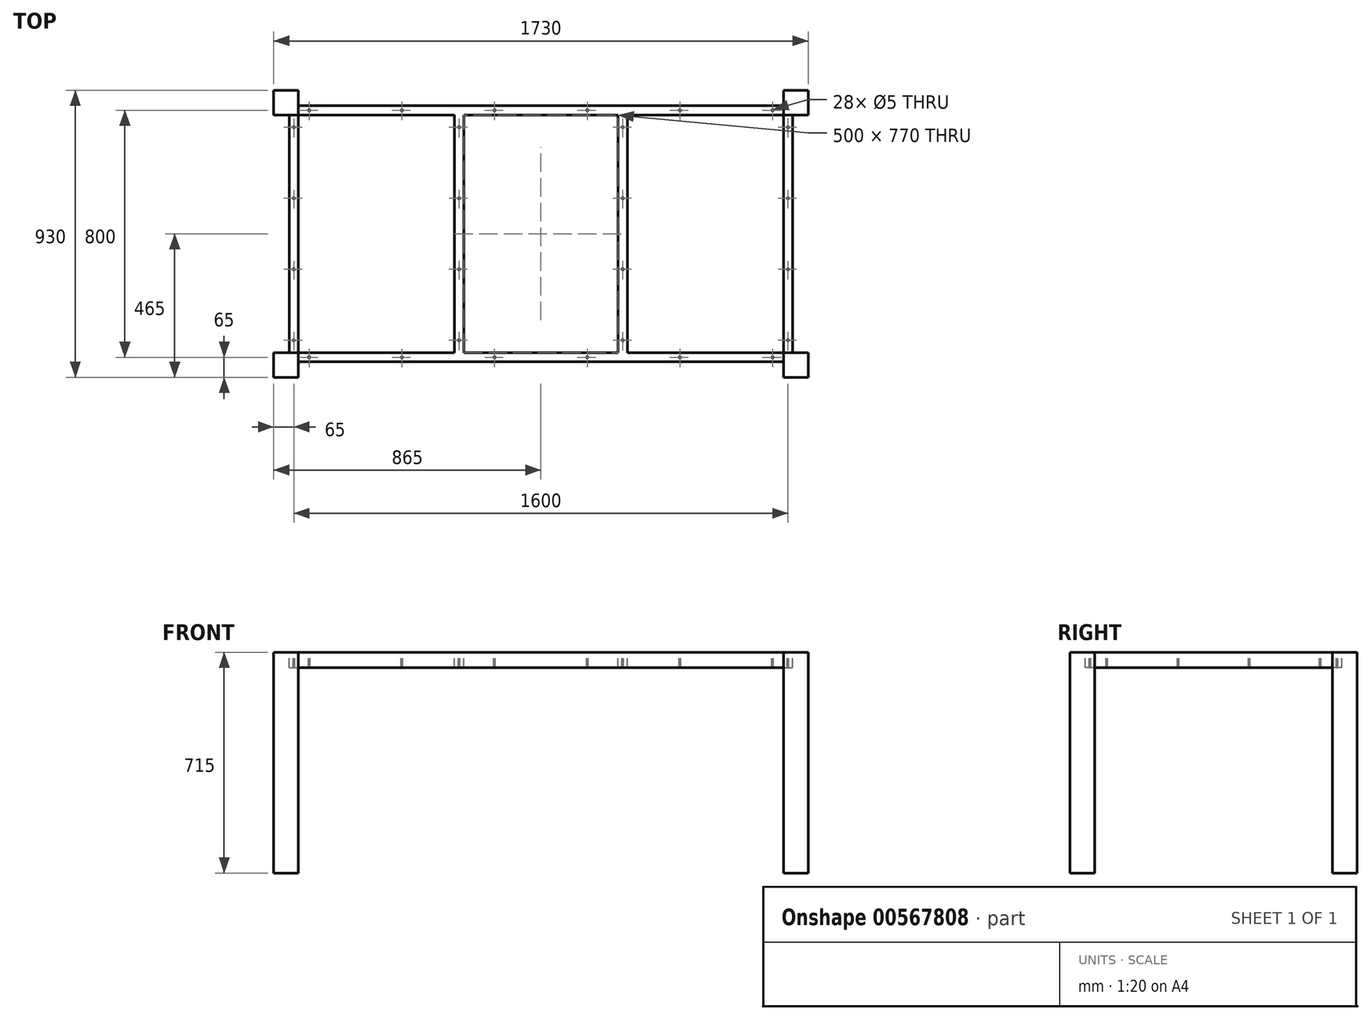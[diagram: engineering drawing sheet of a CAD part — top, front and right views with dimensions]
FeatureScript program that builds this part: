
annotation { "Feature Type Name" : "Feature", "Feature Type Description" : "" }
export const myFeature = defineFeature(function(context is Context, id is Id, definition is map)
    precondition{}
    {
        {
            var Q0;
            Q0=qCreatedBy(makeId("Top.planeOp"),FACE);
            var sketch = newSketch(context, id + "F0", { "sketchPlane" : qUnion([Q0])});
            skLineSegment(sketch, "E0.bottom", {"start": v(-815, 415) * mm, "end": v(815, 415) * mm});
            skLineSegment(sketch, "E0.top", {"start": v(-815, -415) * mm, "end": v(815, -415) * mm});
            skLineSegment(sketch, "E0.left", {"start": v(-815, 415) * mm, "end": v(-815, -415) * mm});
            skLineSegment(sketch, "E0.right", {"start": v(815, 415) * mm, "end": v(815, -415) * mm});
            skPoint(sketch, "E0.middle", {"position": v(0, 0) * mm});
            skLineSegment(sketch, "E1.bottom", {"start": v(-800, 400) * mm, "end": v(800, 400) * mm, "construction": true});
            skLineSegment(sketch, "E1.top", {"start": v(-800, -400) * mm, "end": v(800, -400) * mm, "construction": true});
            skLineSegment(sketch, "E1.left", {"start": v(-800, 400) * mm, "end": v(-800, -400) * mm, "construction": true});
            skLineSegment(sketch, "E1.right", {"start": v(800, 400) * mm, "end": v(800, -400) * mm, "construction": true});
            skLineSegment(sketch, "E2.bottom", {"start": v(-785, 385) * mm, "end": v(785, 385) * mm});
            skLineSegment(sketch, "E2.top", {"start": v(-785, -385) * mm, "end": v(785, -385) * mm});
            skLineSegment(sketch, "E2.left", {"start": v(-785, 385) * mm, "end": v(-785, -385) * mm});
            skLineSegment(sketch, "E2.right", {"start": v(785, 385) * mm, "end": v(785, -385) * mm});
            skLineSegment(sketch, "E3.bottom", {"start": v(785, -385) * mm, "end": v(865, -385) * mm});
            skLineSegment(sketch, "E3.top", {"start": v(785, -465) * mm, "end": v(865, -465) * mm});
            skLineSegment(sketch, "E3.left", {"start": v(785, -385) * mm, "end": v(785, -465) * mm});
            skLineSegment(sketch, "E3.right", {"start": v(865, -385) * mm, "end": v(865, -465) * mm});
            skLineSegment(sketch, "E4.bottom", {"start": v(-865, 465) * mm, "end": v(-785, 465) * mm});
            skLineSegment(sketch, "E4.top", {"start": v(-865, 385) * mm, "end": v(-785, 385) * mm});
            skLineSegment(sketch, "E4.left", {"start": v(-865, 465) * mm, "end": v(-865, 385) * mm});
            skLineSegment(sketch, "E4.right", {"start": v(-785, 465) * mm, "end": v(-785, 385) * mm});
            skLineSegment(sketch, "E5.bottom", {"start": v(785, 465) * mm, "end": v(865, 465) * mm});
            skLineSegment(sketch, "E5.top", {"start": v(785, 385) * mm, "end": v(865, 385) * mm});
            skLineSegment(sketch, "E5.left", {"start": v(785, 465) * mm, "end": v(785, 385) * mm});
            skLineSegment(sketch, "E5.right", {"start": v(865, 465) * mm, "end": v(865, 385) * mm});
            skLineSegment(sketch, "E6.bottom", {"start": v(-865, -385) * mm, "end": v(-785, -385) * mm});
            skLineSegment(sketch, "E6.top", {"start": v(-865, -465) * mm, "end": v(-785, -465) * mm});
            skLineSegment(sketch, "E6.left", {"start": v(-865, -385) * mm, "end": v(-865, -465) * mm});
            skLineSegment(sketch, "E6.right", {"start": v(-785, -385) * mm, "end": v(-785, -465) * mm});
            skPoint(sketch, "E7", {"position": v(-750, -400) * mm});
            skPoint(sketch, "E8", {"position": v(-450, -400) * mm});
            skPoint(sketch, "E9", {"position": v(-150, -400) * mm});
            skPoint(sketch, "E10", {"position": v(150, -400) * mm});
            skPoint(sketch, "E11", {"position": v(450, -400) * mm});
            skPoint(sketch, "E12", {"position": v(750, -400) * mm});
            skPoint(sketch, "E13", {"position": v(800, -345) * mm});
            skPoint(sketch, "E14", {"position": v(800, -115) * mm});
            skPoint(sketch, "E15", {"position": v(800, 115) * mm});
            skPoint(sketch, "E16", {"position": v(800, 345) * mm});
            skPoint(sketch, "E17", {"position": v(750, 400) * mm});
            skPoint(sketch, "E18", {"position": v(450, 400) * mm});
            skPoint(sketch, "E19", {"position": v(150, 400) * mm});
            skPoint(sketch, "E20", {"position": v(-150, 400) * mm});
            skPoint(sketch, "E21", {"position": v(-450, 400) * mm});
            skPoint(sketch, "E22", {"position": v(-750, 400) * mm});
            skPoint(sketch, "E23", {"position": v(-800, 345) * mm});
            skPoint(sketch, "E24", {"position": v(-800, 115) * mm});
            skPoint(sketch, "E25", {"position": v(-800, -115) * mm});
            skPoint(sketch, "E26", {"position": v(-800, -345) * mm});
            skLineSegment(sketch, "E27", {"start": v(-265, 400) * mm, "end": v(-265, -400) * mm, "construction": true});
            skLineSegment(sketch, "E28", {"start": v(-280, 400) * mm, "end": v(-280, -400) * mm});
            skLineSegment(sketch, "E29", {"start": v(-250, -400) * mm, "end": v(-250, 400) * mm});
            skPoint(sketch, "E30", {"position": v(-265, 345) * mm});
            skPoint(sketch, "E31", {"position": v(-265, 115) * mm});
            skPoint(sketch, "E32", {"position": v(-265, -115) * mm});
            skPoint(sketch, "E33", {"position": v(-265, -345) * mm});
            skLineSegment(sketch, "E34", {"start": v(265, 400) * mm, "end": v(265, -400) * mm, "construction": true});
            skLineSegment(sketch, "E35", {"start": v(250, 400) * mm, "end": v(250, -400) * mm});
            skLineSegment(sketch, "E36", {"start": v(280, 400) * mm, "end": v(280, -400) * mm});
            skPoint(sketch, "E37", {"position": v(265, 345) * mm});
            skPoint(sketch, "E38", {"position": v(265, 115) * mm});
            skPoint(sketch, "E39", {"position": v(265, -115) * mm});
            skPoint(sketch, "E40", {"position": v(265, -345) * mm});
            skSolve(sketch);
        }
        {
            var Q0;
            {var subQ0=sQuery(id+"F0.wireOp",EDGE,"E3.top");Q0=makeQuery(id+"F0.imprint","IMPRINT",FACE,{"disambiguationData":[TD([[makeQuery(id+"F0.imprint","IMPRINT",EDGE,{"derivedFrom":subQ0}),1.0]])]});}
            var Q1;
            {var subQ4=sQuery(id+"F0.wireOp",EDGE,"E5.bottom");Q1=makeQuery(id+"F0.imprint","IMPRINT",FACE,{"disambiguationData":[TD([[makeQuery(id+"F0.imprint","IMPRINT",EDGE,{"derivedFrom":subQ4}),-1.0]])]});}
            var Q2;
            {var subQ4=sQuery(id+"F0.wireOp",EDGE,"E4.bottom");Q2=makeQuery(id+"F0.imprint","IMPRINT",FACE,{"disambiguationData":[TD([[makeQuery(id+"F0.imprint","IMPRINT",EDGE,{"derivedFrom":subQ4}),-1.0]])]});}
            var Q3;
            {var subQ0=sQuery(id+"F0.wireOp",EDGE,"E6.top");Q3=makeQuery(id+"F0.imprint","IMPRINT",FACE,{"disambiguationData":[TD([[makeQuery(id+"F0.imprint","IMPRINT",EDGE,{"derivedFrom":subQ0}),1.0]])]});}
            var Q4;
            {var subQ0=sQuery(id+"F0.wireOp",EDGE,"E0.left");var subQ1=sQuery(id+"F0.wireOp",EDGE,"E0.bottom");var subQ2=makeQuery(id+"F0.imprint","INTERSECT",VERTEX,{"derivedFrom":[subQ1,subQ0]});Q4=makeQuery(id+"F0.imprint","IMPRINT",FACE,{"disambiguationData":[TD([[makeQuery(id+"F0.imprint","IMPRINT",EDGE,{"disambiguationData":[TD([[subQ2,-1.0]])],"derivedFrom":subQ1}),-1.0]])]});}
            var Q5;
            {var subQ0=sQuery(id+"F0.wireOp",EDGE,"E0.left");var subQ1=sQuery(id+"F0.wireOp",EDGE,"E0.top");var subQ2=makeQuery(id+"F0.imprint","INTERSECT",VERTEX,{"derivedFrom":[subQ1,subQ0]});Q5=makeQuery(id+"F0.imprint","IMPRINT",FACE,{"disambiguationData":[TD([[makeQuery(id+"F0.imprint","IMPRINT",EDGE,{"disambiguationData":[TD([[subQ2,-1.0]])],"derivedFrom":subQ1}),1.0]])]});}
            var Q6;
            {var subQ0=sQuery(id+"F0.wireOp",EDGE,"E0.right");var subQ1=sQuery(id+"F0.wireOp",EDGE,"E0.top");var subQ2=makeQuery(id+"F0.imprint","INTERSECT",VERTEX,{"derivedFrom":[subQ1,subQ0]});Q6=makeQuery(id+"F0.imprint","IMPRINT",FACE,{"disambiguationData":[TD([[makeQuery(id+"F0.imprint","IMPRINT",EDGE,{"disambiguationData":[TD([[subQ2,1.0]])],"derivedFrom":subQ1}),1.0]])]});}
            var Q7;
            {var subQ0=sQuery(id+"F0.wireOp",EDGE,"E0.right");var subQ1=sQuery(id+"F0.wireOp",EDGE,"E0.bottom");var subQ2=makeQuery(id+"F0.imprint","INTERSECT",VERTEX,{"derivedFrom":[subQ1,subQ0]});Q7=makeQuery(id+"F0.imprint","IMPRINT",FACE,{"disambiguationData":[TD([[makeQuery(id+"F0.imprint","IMPRINT",EDGE,{"disambiguationData":[TD([[subQ2,1.0]])],"derivedFrom":subQ1}),-1.0]])]});}
            extrude(context, id + "F1", {"entities" : qUnion([Q0, Q1, Q2, Q3, Q4, Q5, Q6, Q7]), "oppositeDirection" : true, "depth" : 715 * mm, "offsetDistance" : 25 * mm});
        }
        {
            var Q0;
            {var subQ5=sQuery(id+"F0.wireOp",EDGE,"E2.bottom");Q0=makeQuery(id+"F0.imprint","IMPRINT",FACE,{"disambiguationData":[TD([[makeQuery(id+"F0.imprint","IMPRINT",EDGE,{"derivedFrom":subQ5}),1.0]])]});}
            var Q1;
            {var subQ5=sQuery(id+"F0.wireOp",EDGE,"E2.left");Q1=makeQuery(id+"F0.imprint","IMPRINT",FACE,{"disambiguationData":[TD([[makeQuery(id+"F0.imprint","IMPRINT",EDGE,{"derivedFrom":subQ5}),-1.0]])]});}
            var Q2;
            {var subQ5=sQuery(id+"F0.wireOp",EDGE,"E2.right");Q2=makeQuery(id+"F0.imprint","IMPRINT",FACE,{"disambiguationData":[TD([[makeQuery(id+"F0.imprint","IMPRINT",EDGE,{"derivedFrom":subQ5}),1.0]])]});}
            var Q3;
            {var subQ5=sQuery(id+"F0.wireOp",EDGE,"E2.top");Q3=makeQuery(id+"F0.imprint","IMPRINT",FACE,{"disambiguationData":[TD([[makeQuery(id+"F0.imprint","IMPRINT",EDGE,{"derivedFrom":subQ5}),-1.0]])]});}
            var Q4;
            {var subQ0=sQuery(id+"F0.wireOp",EDGE,"E35");var subQ1=sQuery(id+"F0.wireOp",EDGE,"E2.bottom");var subQ2=makeQuery(id+"F0.imprint","INTERSECT",VERTEX,{"derivedFrom":[subQ1,subQ0]});Q4=makeQuery(id+"F0.imprint","IMPRINT",FACE,{"disambiguationData":[TD([[makeQuery(id+"F0.imprint","IMPRINT",EDGE,{"disambiguationData":[TD([[subQ2,-1.0]])],"derivedFrom":subQ1}),-1.0]])]});}
            var Q5;
            {var subQ0=sQuery(id+"F0.wireOp",EDGE,"E28");var subQ1=sQuery(id+"F0.wireOp",EDGE,"E2.bottom");var subQ2=makeQuery(id+"F0.imprint","INTERSECT",VERTEX,{"derivedFrom":[subQ1,subQ0]});Q5=makeQuery(id+"F0.imprint","IMPRINT",FACE,{"disambiguationData":[TD([[makeQuery(id+"F0.imprint","IMPRINT",EDGE,{"disambiguationData":[TD([[subQ2,-1.0]])],"derivedFrom":subQ1}),-1.0]])]});}
            extrude(context, id + "F2", {"entities" : qUnion([Q0, Q1, Q2, Q3, Q4, Q5]), "oppositeDirection" : true, "depth" : 50 * mm, "offsetDistance" : 25 * mm});
        }
        {
            var Q0;
            Q0=sQuery(id+"F0.wireOp",VERTEX,"E21");
            var Q1;
            Q1=sQuery(id+"F0.wireOp",VERTEX,"E20");
            var Q2;
            Q2=sQuery(id+"F0.wireOp",VERTEX,"E19");
            var Q3;
            Q3=sQuery(id+"F0.wireOp",VERTEX,"E18");
            var Q4;
            Q4=sQuery(id+"F0.wireOp",VERTEX,"E16");
            var Q5;
            Q5=sQuery(id+"F0.wireOp",VERTEX,"E17");
            var Q6;
            Q6=sQuery(id+"F0.wireOp",VERTEX,"E22");
            var Q7;
            Q7=sQuery(id+"F0.wireOp",VERTEX,"E23");
            var Q8;
            Q8=sQuery(id+"F0.wireOp",VERTEX,"E24");
            var Q9;
            Q9=sQuery(id+"F0.wireOp",VERTEX,"E25");
            var Q10;
            Q10=sQuery(id+"F0.wireOp",VERTEX,"E26");
            var Q11;
            Q11=sQuery(id+"F0.wireOp",VERTEX,"E7");
            var Q12;
            Q12=sQuery(id+"F0.wireOp",VERTEX,"E8");
            var Q13;
            Q13=sQuery(id+"F0.wireOp",VERTEX,"E9");
            var Q14;
            Q14=sQuery(id+"F0.wireOp",VERTEX,"E10");
            var Q15;
            Q15=sQuery(id+"F0.wireOp",VERTEX,"E11");
            var Q16;
            Q16=sQuery(id+"F0.wireOp",VERTEX,"E12");
            var Q17;
            Q17=sQuery(id+"F0.wireOp",VERTEX,"E14");
            var Q18;
            Q18=sQuery(id+"F0.wireOp",VERTEX,"E13");
            var Q19;
            Q19=sQuery(id+"F0.wireOp",VERTEX,"E15");
            var Q20;
            Q20=sQuery(id+"F0.wireOp",VERTEX,"E30");
            var Q21;
            Q21=sQuery(id+"F0.wireOp",VERTEX,"E31");
            var Q22;
            Q22=sQuery(id+"F0.wireOp",VERTEX,"E32");
            var Q23;
            Q23=sQuery(id+"F0.wireOp",VERTEX,"E33");
            var Q24;
            Q24=sQuery(id+"F0.wireOp",VERTEX,"E40");
            var Q25;
            Q25=sQuery(id+"F0.wireOp",VERTEX,"E39");
            var Q26;
            Q26=sQuery(id+"F0.wireOp",VERTEX,"E38");
            var Q27;
            Q27=sQuery(id+"F0.wireOp",VERTEX,"E37");
            var Q28;
            Q28=makeQuery(id+"F2.opExtrude","SWEPT_BODY",BODY,{"disambiguationData":[OSD([sQuery(id+"F0.wireOp",EDGE,"E0.bottom"),sQuery(id+"F0.wireOp",EDGE,"E2.bottom"),sQuery(id+"F0.wireOp",EDGE,"E4.right"),sQuery(id+"F0.wireOp",EDGE,"E5.left")])]});
            var Q29;
            Q29=makeQuery(id+"F2.opExtrude","SWEPT_BODY",BODY,{"disambiguationData":[OSD([sQuery(id+"F0.wireOp",EDGE,"E0.right"),sQuery(id+"F0.wireOp",EDGE,"E2.right"),sQuery(id+"F0.wireOp",EDGE,"E3.bottom"),sQuery(id+"F0.wireOp",EDGE,"E5.top")])]});
            var Q30;
            Q30=makeQuery(id+"F2.opExtrude","SWEPT_BODY",BODY,{"disambiguationData":[OSD([sQuery(id+"F0.wireOp",EDGE,"E0.left"),sQuery(id+"F0.wireOp",EDGE,"E2.left"),sQuery(id+"F0.wireOp",EDGE,"E4.top"),sQuery(id+"F0.wireOp",EDGE,"E6.bottom")])]});
            var Q31;
            Q31=makeQuery(id+"F2.opExtrude","SWEPT_BODY",BODY,{"disambiguationData":[OSD([sQuery(id+"F0.wireOp",EDGE,"E0.top"),sQuery(id+"F0.wireOp",EDGE,"E2.top"),sQuery(id+"F0.wireOp",EDGE,"E3.left"),sQuery(id+"F0.wireOp",EDGE,"E6.right")])]});
            hole(context, id + "F3", {"style" : HoleStyle.SIMPLE, "endStyle" : HoleEndStyle.THROUGH, "holeDiameter" : 5 * mm, "isTappedThrough" : true, "tappedDepth" : 12 * mm, "tapClearance" : 3, "startFromSketch" : true, "locations" : qUnion([Q0, Q1, Q2, Q3, Q4, Q5, Q6, Q7, Q8, Q9, Q10, Q11, Q12, Q13, Q14, Q15, Q16, Q17, Q18, Q19, Q20, Q21, Q22, Q23, Q24, Q25, Q26, Q27]), "scope" : qUnion([Q28, Q29, Q30, Q31]), "majorDiameter" : 5 * mm});
        }
    });
